# Revit family: AIRTECNICS_AIR CURTAIN_ROTOWIND_DX-VRV_(DAIKIN) - (False Ceiling Mounting)_00
name_source: partatom
category: Mechanical Equipment
revit_build: Autodesk Revit 2016 (Build: 20150714_1515(x64)
units: mm (PartAtom-declared; Revit-internal decimal feet)

## family parameters
Always vertical = Yes
Cut with Voids When Loaded = No
OmniClass Number = 23.75.70.21.17
OmniClass Title = Air Curtains
Part Type = Normal
Room Calculation Point = No
Round Connector Dimension = Use Diameter
Shared = No
Work Plane-Based = No

## types (2) — shared parameters
BIMETRICAL = http://www.bimetrical.com
BIMETRICAL Category = Coil
Cable = CB7
Depth = 360 mm
EC = Yes
Family Version = 1.0
Fans Stage = 5
Frequency = 50 Hz
G = Yes
Height = 285 mm  [stored 0.935039 ft]
IfcExportAs = IfcCoilType
IfcExportType = DXCOOLINGCOIL
Manufacturer = AIRTECNICS
Model = Air curtain Rotowind ECG DX/VRV DA
Name_Lookup_Data = ROTOWIND_(DX)_DA_Data_Lookup
Name_Lookup_Data2 = ROTOWIND_(DX)_DA_Mainfolds_Lookup
Name_Lookup_Data3 = ROTOWIND_(DX)_DA_ExpValve_Lookup
Name_Lookup_Ref = ROTOWIND_(DX)_DA_Ref_Lookup
Name_Lookup_Ref_EU = ROTOWIND_(DX)_DA_Ref_EU_Lookup
Remote Control = -
Review Date = 02/19
Revit Version = Revit 2016 - English
Type Comments = Energy saving heat pump air curtain: Up to 70% reduction in costs and CO2 emissions (heating mode).
Specially designed to be installed in all type of revolving doors. Two possible layouts, tailored dimensions.
Self-supporting casing construction made of galvanized steel plate, finished in structural epoxy-polyester painting white colour RAL9016 as standard. Other colours or stainless steel are available on request. 
Large faceted inlet grille avoiding intensive maintenance. 
Circular anodized aluminium outlet vanes, airfoil shaped.
Double-inlet centrifugal fans driven by an external rotor motor and low noise level. 5-speed selector. EC models assembled with very low consumption efficiency fans. 
Includes only heating direct expansion coil with installed temperature sensors. Under request it can be modified to work in cooling and heating mode (not recomended) with optional condensate water pump.
Plug&Play control panel CS-5DX-NE slave DX with 5 speeds selector and 7m telephone cable included.
DX 1:1:
Ready to connect to DAIKIN Inverter outdoor heat pump unit (R410A) and  expansion valve not included, the customer should purchase it.
Requires  DAIKIN DX Interface KIT adapted for air curtain and  programmable control, please consult.
DX VRV:
Ready to connect to DAIKIN VRV outdoor heat pump unit (R410A) and  expansion valve not included, the customer should purchase it.
Requires  DAIKIN VRV Interface KIT adapted for air curtain and  programmable control, please consult.
Type Image = <None>
URL = https://www.airtecnics.com
URL_Datasheet = https://www.airtecnics.com
URL_Manufacturer = https://www.airtecnics.com
· HEATING · = -/ Select Heating /-

## per-type parameters (varying)
| type | DX 1:1 | DX VRV |
| ROTOWIND ECG VRV-DA - (False Ceiling Mounting) | No | Yes |
| ROTOWIND ECG DX-DA - (False Ceiling Mounting) | Yes | No |

note: [stored X ft] marks values corroborated as IEEE doubles in the binary element streams (Revit-internal decimal feet)
